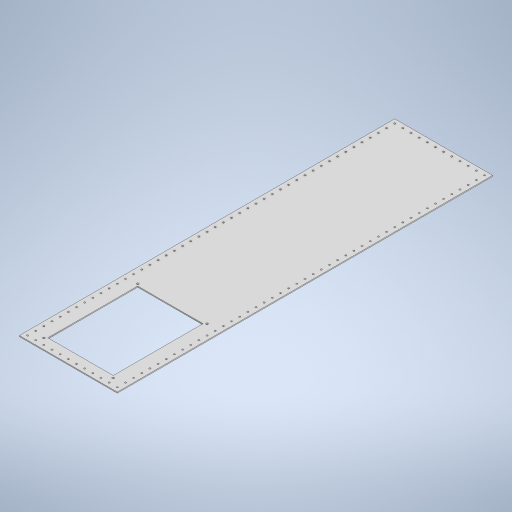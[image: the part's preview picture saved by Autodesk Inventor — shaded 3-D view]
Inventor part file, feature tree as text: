
AUTODESK INVENTOR PART (.ipt)
format: ipt  version: 2023.4 (Build 274418000, 418)  size: 440,320 bytes
history: native  units: in
note: dims shown in document units (in); Inventor stores cm internally (conversion verified against a paired STEP export)
features: extrude x2, sketch x2, sheet_metal_op x1, other x1
ambient origin geometry x8: Origin, YZ Plane, XZ Plane, XY Plane, X Axis, Y Axis, Z Axis, Center Point
bodies: Body1 (feature_tree)
feature tree (6):
  sheet_metal_op  "Face2"
  extrude  "Extrusion6"  Depth=12.0in
  extrude  "Extrusion7"  Depth=1.5in
  other  "Plate2"
  sketch  "Sketch4"  dims[d0=46.0in d1=12.0in]
  sketch  "Sketch5"  dims[d3=0.197in d4=0.5in d5=0.5in d6=0.197in d7=0.5in d8=0.5in d9=4.7244in d11=1.0in d12=0.3937in d14=1.0in d16=18.1102in d18=1.0in d19=0.3937in d21=1.0in d23=4.7244in d25=1.0in d26=0.3937in d28=1.0in d30=17.7165in d32=1.0in d33=0.3937in d35=1.0in d37=0.125in d83=8.0in d84=11.0in d85=2.0in d86=2.0in d87=1.5in d88=1.0in d89=0.0in d90=0.25in d91=1.25in d92=1.75in d93=0.25in d94=1.75in d95=12.75in d96=0.25in d97=1.75in d98=1.25in d99=0.25in d100=1.75in d101=12.75in d102=1.0in d103=0.0in d49=0.5in d50=0.0344in d51=0.5in d52=0.0344in]
